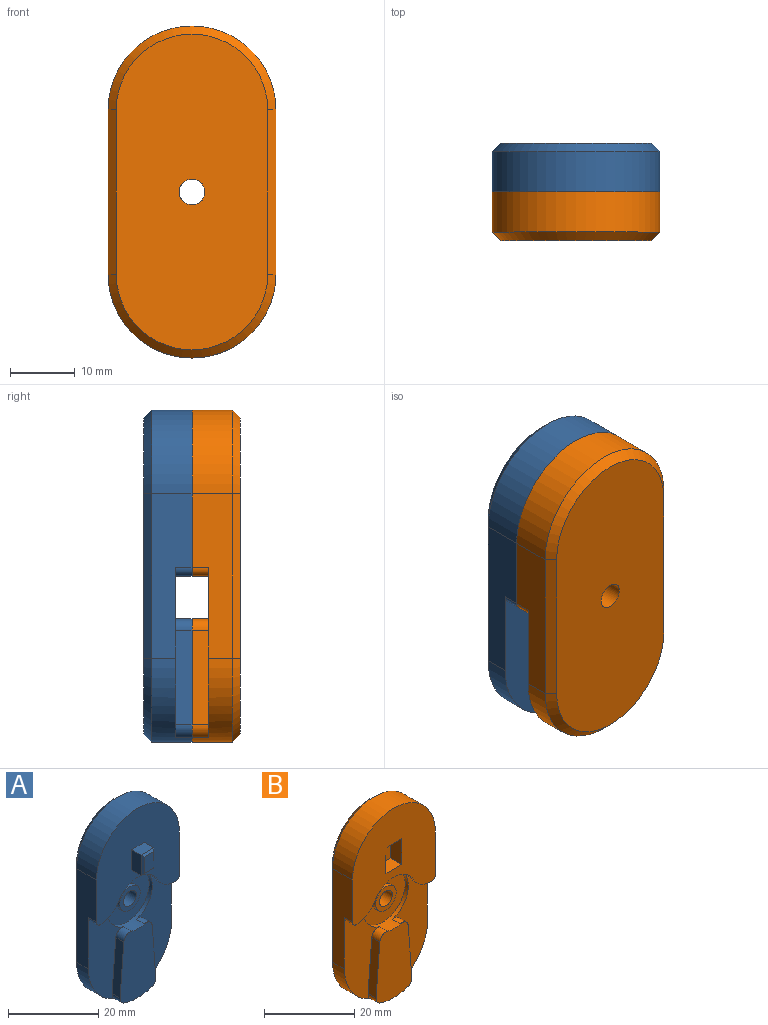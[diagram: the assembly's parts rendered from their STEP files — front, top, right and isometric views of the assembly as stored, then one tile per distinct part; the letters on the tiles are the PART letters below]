
ASSEMBLY  parts=2 mates=1
PART A: 39 faces, bbox 26x11x51.4 mm
  f0: plane 19.07x11.23mm, normal (0,-1,0), area 184.9mm2, adj f7,f10,f24,f25,f26,f27,f28,f29
  f1: plane 28.2x11mm, normal (0,-1,0), area 170.5mm2, adj f4,f7,f10,f14,f21,f23,f24,f26
  f2: plane 28.2x11mm, normal (0,-1,0), area 170.5mm2, adj f6,f7,f10,f13,f20,f22,f25,f27
  f3: plane 14x14mm, normal (0,-1,0), area 121.8mm2, adj f10,f11
  f4: plane 25.4x6.23mm, normal (1,0,0), area 123.3mm2, adj f1,f5,f7,f15,f18,f23
  f5: cylinder r=13mm len=26mm, axis (0,-1,0), area 254.4mm2, adj f4,f6,f15,f16
  f6: plane 25.4x6.23mm, normal (-1,0,0), area 123.3mm2, adj f2,f5,f7,f15,f17,f22
  f7: cylinder r=13mm len=26mm, axis (0,-1,0), area 174.5mm2, adj f0,f1,f2,f4,f6,f19,f28,f29
  f8: cylinder r=2mm len=5mm, axis (0,-1,0), area 62.8mm2, adj f9,f12
  f9: plane 48.86x23.46mm, normal (0,1,0), area 1015.6mm2, adj f8,f16,f17,f18,f19
  f10: cylinder r=7mm len=14mm, axis (0,1,0), area 92.2mm2, adj f0,f1,f2,f3,f15,f20,f21,f26
  f11: cylinder r=3.2mm len=6.4mm, axis (0,1,0), area 20.1mm2, adj f3,f12
  f12: plane 6.4x6.4mm, normal (0,-1,0), area 19.6mm2, adj f8,f11
  f13: plane 2.5x0.15mm, normal (0,0,-1), area 0.4mm2, adj f2,f15,f20,f22
  f14: plane 2.5x0.15mm, normal (0,0,-1), area 0.4mm2, adj f1,f15,f21,f23
  f15: plane 26x25.7mm, normal (0,-1,0), area 489.5mm2, adj f4,f5,f6,f10,f13,f14,f20,f21
  f16: cone r=13mm half-angle=45deg, axis (0,-1,0), area 69.8mm2, adj f5,f9,f17,f18
  f17: plane 25.4x1.27mm, normal (-0.71,0.71,0), area 45.6mm2, adj f6,f9,f16,f19
  f18: plane 25.4x1.27mm, normal (0.71,0.71,0), area 45.6mm2, adj f4,f9,f16,f19
  f19: cone r=13mm half-angle=45deg, axis (0,-1,0), area 69.8mm2, adj f7,f9,f17,f18
  f20: cylinder r=6.07mm len=5.38mm, axis (0,1,0), area 16.5mm2, adj f2,f10,f13,f15
  f21: cylinder r=6.07mm len=5.38mm, axis (0,1,0), area 16.5mm2, adj f1,f10,f14,f15
  f22: cylinder r=1.27mm len=2.5mm, axis (0,1,0), area 5mm2, adj f2,f6,f13,f15
  f23: cylinder r=1.27mm len=2.5mm, axis (0,1,0), area 5mm2, adj f1,f4,f14,f15
  f24: plane 14.62x2.5mm, normal (1,0,0.08), area 36.7mm2, adj f0,f1,f26,f29
  f25: plane 14.62x2.5mm, normal (-1,0,0.08), area 36.7mm2, adj f0,f2,f27,f28
  f26: cylinder r=1.91mm len=2.5mm, axis (0,1,0), area 8.5mm2, adj f0,f1,f10,f24
  f27: cylinder r=1.91mm len=2.5mm, axis (0,1,0), area 8.5mm2, adj f0,f2,f10,f25
  f28: cylinder r=1.91mm len=2.5mm, axis (0,-1,0), area 6.2mm2, adj f0,f2,f7,f25
  f29: cylinder r=1.91mm len=2.5mm, axis (0,-1,0), area 6.2mm2, adj f0,f1,f7,f24
  f30: plane 4x2.99mm, normal (0,0,-1), area 12mm2, adj f15,f31,f33,f37
  f31: plane 5.5x2.99mm, normal (1,0,0), area 16.5mm2, adj f15,f30,f32,f35
  f32: plane 4x2.99mm, normal (0,0,1), area 12mm2, adj f15,f31,f33,f36
  f33: plane 5.5x2.99mm, normal (-1,0,0), area 16.5mm2, adj f15,f30,f32,f38
  f34: plane 4.48x2.98mm, normal (0,-1,0), area 13.4mm2, adj f35,f36,f37,f38
  f35: plane 5.5x0.51mm, normal (0.71,-0.71,0), area 3.6mm2, adj f31,f34,f36,f37
  f36: plane 4x0.51mm, normal (0,-0.71,0.71), area 2.5mm2, adj f32,f34,f35,f38
  f37: plane 4x0.51mm, normal (0,-0.71,-0.71), area 2.5mm2, adj f30,f34,f35,f38
  f38: plane 5.5x0.51mm, normal (-0.71,-0.71,0), area 3.6mm2, adj f33,f34,f36,f37
PART B: 35 faces, bbox 26x7.5x51.4 mm
  f0: plane 19.07x11.23mm, normal (0,-1,0), area 184.9mm2, adj f7,f10,f29,f30,f31,f32,f33,f34
  f1: plane 28.2x11mm, normal (0,-1,0), area 170.5mm2, adj f4,f7,f10,f14,f26,f28,f29,f31
  f2: plane 28.2x11mm, normal (0,-1,0), area 170.5mm2, adj f6,f7,f10,f13,f25,f27,f30,f32
  f3: plane 14x14mm, normal (0,-1,0), area 121.8mm2, adj f10,f11
  f4: plane 25.4x6.23mm, normal (1,0,0), area 123.3mm2, adj f1,f5,f7,f15,f23,f28
  f5: cylinder r=13mm len=26mm, axis (0,-1,0), area 254.4mm2, adj f4,f6,f15,f21
  f6: plane 25.4x6.23mm, normal (-1,0,0), area 123.3mm2, adj f2,f5,f7,f15,f22,f27
  f7: cylinder r=13mm len=26mm, axis (0,-1,0), area 174.5mm2, adj f0,f1,f2,f4,f6,f24,f33,f34
  f8: cylinder r=2mm len=5mm, axis (0,-1,0), area 62.8mm2, adj f9,f12
  f9: plane 48.86x23.46mm, normal (0,1,0), area 1015.6mm2, adj f8,f21,f22,f23,f24
  f10: cylinder r=7mm len=14mm, axis (0,1,0), area 92.2mm2, adj f0,f1,f2,f3,f15,f25,f26,f31
  f11: cylinder r=3.2mm len=6.4mm, axis (0,1,0), area 20.1mm2, adj f3,f12
  f12: plane 6.4x6.4mm, normal (0,-1,0), area 19.6mm2, adj f8,f11
  f13: plane 2.5x0.15mm, normal (0,0,-1), area 0.4mm2, adj f2,f15,f25,f27
  f14: plane 2.5x0.15mm, normal (0,0,-1), area 0.4mm2, adj f1,f15,f26,f28
  f15: plane 26x25.7mm, normal (0,-1,0), area 476.5mm2, adj f4,f5,f6,f10,f13,f14,f17,f18
  f16: plane 7x5mm, normal (0,-1,0), area 35mm2, adj f17,f18,f19,f20
  f17: plane 5x3.5mm, normal (0,0,1), area 17.5mm2, adj f15,f16,f18,f20
  f18: plane 7x3.5mm, normal (-1,0,0), area 24.5mm2, adj f15,f16,f17,f19
  f19: plane 5x3.5mm, normal (0,0,-1), area 17.5mm2, adj f15,f16,f18,f20
  f20: plane 7x3.5mm, normal (1,0,0), area 24.5mm2, adj f15,f16,f17,f19
  f21: cone r=13mm half-angle=45deg, axis (0,-1,0), area 69.8mm2, adj f5,f9,f22,f23
  f22: plane 25.4x1.27mm, normal (-0.71,0.71,0), area 45.6mm2, adj f6,f9,f21,f24
  f23: plane 25.4x1.27mm, normal (0.71,0.71,0), area 45.6mm2, adj f4,f9,f21,f24
  f24: cone r=13mm half-angle=45deg, axis (0,-1,0), area 69.8mm2, adj f7,f9,f22,f23
  f25: cylinder r=6.07mm len=5.38mm, axis (0,1,0), area 16.5mm2, adj f2,f10,f13,f15
  f26: cylinder r=6.07mm len=5.38mm, axis (0,1,0), area 16.5mm2, adj f1,f10,f14,f15
  f27: cylinder r=1.27mm len=2.5mm, axis (0,1,0), area 5mm2, adj f2,f6,f13,f15
  f28: cylinder r=1.27mm len=2.5mm, axis (0,1,0), area 5mm2, adj f1,f4,f14,f15
  f29: plane 14.62x2.5mm, normal (1,0,0.08), area 36.7mm2, adj f0,f1,f31,f34
  f30: plane 14.62x2.5mm, normal (-1,0,0.08), area 36.7mm2, adj f0,f2,f32,f33
  f31: cylinder r=1.91mm len=2.5mm, axis (0,1,0), area 8.5mm2, adj f0,f1,f10,f29
  f32: cylinder r=1.91mm len=2.5mm, axis (0,1,0), area 8.5mm2, adj f0,f2,f10,f30
  f33: cylinder r=1.91mm len=2.5mm, axis (0,-1,0), area 6.2mm2, adj f0,f2,f7,f30
  f34: cylinder r=1.91mm len=2.5mm, axis (0,-1,0), area 6.2mm2, adj f0,f1,f7,f29
PLACE A t=(-16.42,-1.77,9.32)mm
PLACE B rot(axis=(0,0,1),180deg) t=(-16.42,-8.77,9.32)mm
MATE fastened B.f8 <-> A.f8  axis (0,1,0) through (-16.42,-5.27,9.32)mm
